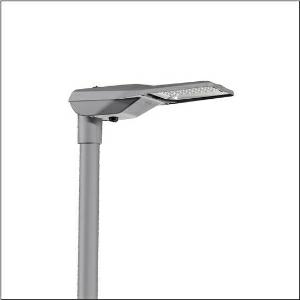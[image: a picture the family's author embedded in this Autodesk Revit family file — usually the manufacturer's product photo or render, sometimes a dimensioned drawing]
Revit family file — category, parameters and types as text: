
# Revit family: streetlight_sl_21_iq_mini___p1_0a_5xe2a31y08hb_fafd
name_source: partatom
category: Lighting Fixtures
units: mm (PartAtom-declared; Revit-internal decimal feet)

## family parameters
Cut with Voids When Loaded = No
Host = Face
Light Source = No
Part Type = Normal
Room Calculation Point = No
Round Connector Dimension = Use Diameter
Shared = No

## types (1)
- --- (1 x LED, 9750 lm, 71 W, 3000K)
    Apparent Load = 71 VA
    CIE Flux Codes = 21 50 90 100 100
    Color Rendering = 70
    Color Temperature = 3000K
    Default Elevation = 1800 mm
    Description = Streetlight SL 21 iQ mini, mast luminaire, primary light control with lens, of PMMA, primary optical cover: cover, of toughened safety glass, transparent, light distribution: P1.0a, light emission: direct distribution, primary light characteristic: asymmetric, installation type: post-top, side-entry, LED, High Power LED, rated luminous flux: 9.750lm, luminous efficacy: 137lm/W, light colour: 730, colour temperature: 3000K, control gear: iQ-Street Remote, D4i with power reduction, control: pre-setting: logarithmic dimming characteristic, Street-Remote, Auto-Match, Temp-Guard, Lumen-Switch, Night-Set, Smart-Wire, Light-Fading, Desk-Remote (wireless, voltage-free reading and setting of iQ features in the workshop via application-optimized NFC function/RFID function), optimised constant luminous flux control (CLO 2.0), mains connection: 220..240V, AC, 50/60Hz, start of lifetime: 71W, end of service life: 75W, reduction: 30W, luminaire housing, of diecast aluminium, powder-coated, Siteco® metallic grey (DB 702S), corrosivity category C5 mid according to DIN EN ISO 12944, please order mast flange separately, inclination adjustable: 0°, 5°, 10°, 15°, sealing non-destructively replaceable, multi-level sealing system, length: 628mm, width: 235mm, height: 110mm, mast flange for spigot size: 42mm (side-entry): 5XC10008XM4, 60/48mm (side-entry/post-top): 5XC10108XM2, 76/60mm (side-entry/post-top): 5XC10108XM1, mounting height: 4..8m, Smart Interface below and above, protection rating (complete): IP66, insulation class (complete): insulation class II (safety insulation), certification: CE, ENEC, ENEC+, VDE, impact resistance: IK10, permissible operating ambient temperature for outdoor applications: -40..+50°C, standard-compliant lighting for roads and squares, packaging unit: 1 piece

Light Distribution: P1.0a
    Height = 110 mm
    Lamp = 1 x LED
    Lamp Light Flux = 9750 lm
    Lamp Power = 71 W
    Lamp count = 1
    Length = 625 mm
    Luminous efficacy = 137 lm/W
    Manufacturer = Siteco
    ModVariant = No
    Model = 5XE2A31Y08HB
    Number of Poles = 1
    OnlyDefault = Yes
    Power Factor = 1
    Product Name = Streetlight SL 21 iQ mini | P1.0a
    Product group = mast luminaire | pylon top
    ProductGroupID = 6100
    Protection Class = Protection class II
    Protection Degree = IP 66
    RLX_Detail_Level = 1
    RLX_Emergency_Light_Flux = 0 lm
    RLX_Emergency_Type = 0
    RLX_Emergency_Type_DB = No
    RlxData = <blob elided: 37853 chars, md5=9ef1843c>
    Socket = socket
    Standby Power = 0 W
    System Light Flux = 9750 lm
    System Power = 71 W
    Type Comments = factory setting: luminous flux: 100 % | dim-lin: 254 | 716 mA
    Type Image = l_1003514.jpg
    URL = http://relux.com
    VarID = @adj_113500
    Voltage = 0 V
    Weight = 0.00 kg
    Width = 234 mm

## geometry (parser evidence)
native form markers: Blend x4, Sweep x10
no freeform markers — native parametric forms only
